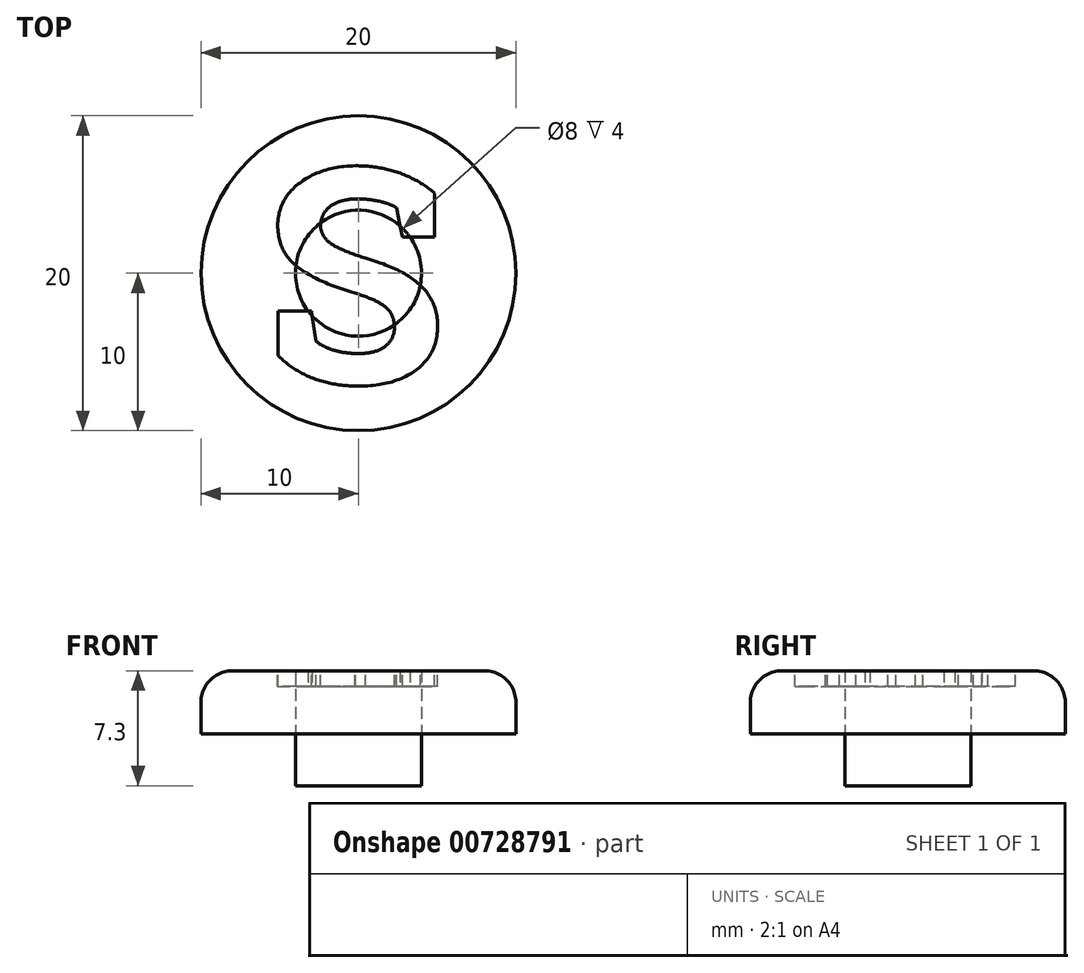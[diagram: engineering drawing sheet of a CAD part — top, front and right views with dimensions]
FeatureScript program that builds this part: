
annotation { "Feature Type Name" : "Feature", "Feature Type Description" : "" }
export const myFeature = defineFeature(function(context is Context, id is Id, definition is map)
    precondition{}
    {
        {
            var Q0;
            Q0=qCreatedBy(makeId("Top.planeOp"),FACE);
            var sketch = newSketch(context, id + "F0", { "sketchPlane" : qUnion([Q0])});
            skCircle(sketch, "E0", {"center": v(0, 0) * mm, "radius": 4 * mm});
            skCircle(sketch, "E1.0", {"center": v(0, 0) * mm, "radius": 10 * mm});
            skSolve(sketch);
        }
        {
            var Q0;
            Q0=makeQuery(id+"F0.imprint","IMPRINT",FACE,{"disambiguationData":[TD([[makeQuery(id+"F0.imprint","IMPRINT",EDGE,{"derivedFrom":sQuery(id+"F0.wireOp",EDGE,"E0")}),1.0]])]});
            extrude(context, id + "F1", {"entities" : qUnion([Q0]), "oppositeDirection" : true, "depth" : 3.3 * mm, "offsetDistance" : 25.4 * mm});
        }
        {
            var Q0;
            Q0 = qSketchRegion(id + "F0", true);
            extrude(context, id + "F2", {"entities" : qUnion([Q0]), "operationType" : NewBodyOperationType.ADD, "depth" : 4 * mm, "offsetDistance" : 25.4 * mm});
        }
        {
            var Q0;
            Q0=makeQuery(id+"F1.opExtrude","CAP_FACE",FACE,{"disambiguationData":[OSD([sQuery(id+"F0.wireOp",EDGE,"E0")])],"isStart":true});
            extrude(context, id + "F3", {"entities" : qUnion([Q0]), "depth" : 4 * mm, "offsetDistance" : 25.4 * mm});
        }
        {
            var Q0;
            Q0=makeQuery(id+"F2.opExtrude","CAP_EDGE",EDGE,{"disambiguationData":[OSD([sQuery(id+"F0.wireOp",EDGE,"E1.0")])],"isStart":false});
            fillet(context, id + "F4", {"entities" : qUnion([Q0]), "radius" : 2 * mm, "tangentPropagation" : true, "allowEdgeOverflow" : false});
        }
        {
            var Q0;
            Q0=makeQuery(id+"F2.opExtrude","CAP_FACE",FACE,{"disambiguationData":[OSD([sQuery(id+"F0.wireOp",EDGE,"E0"),sQuery(id+"F0.wireOp",EDGE,"E1.0")])],"isStart":false});
            var sketch = newSketch(context, id + "F5", { "sketchPlane" : qUnion([Q0])});
            skText(sketch, "E2", { "text": "S", "fontName": "RobotoSlab-Bold.ttf"});
            const initialGuessF5  = {"E2": [-0.00603, -0.00697, 1, 0, 0.01378]};
            skSetInitialGuess(sketch, initialGuessF5);
            skSolve(sketch);
        }
        {
            var Q0;
            Q0 = qSketchRegion(id + "F5", true);
            extrude(context, id + "F6", {"entities" : qUnion([Q0]), "operationType" : NewBodyOperationType.REMOVE, "oppositeDirection" : true, "depth" : 1 * mm, "offsetDistance" : 25.4 * mm});
        }
    });
